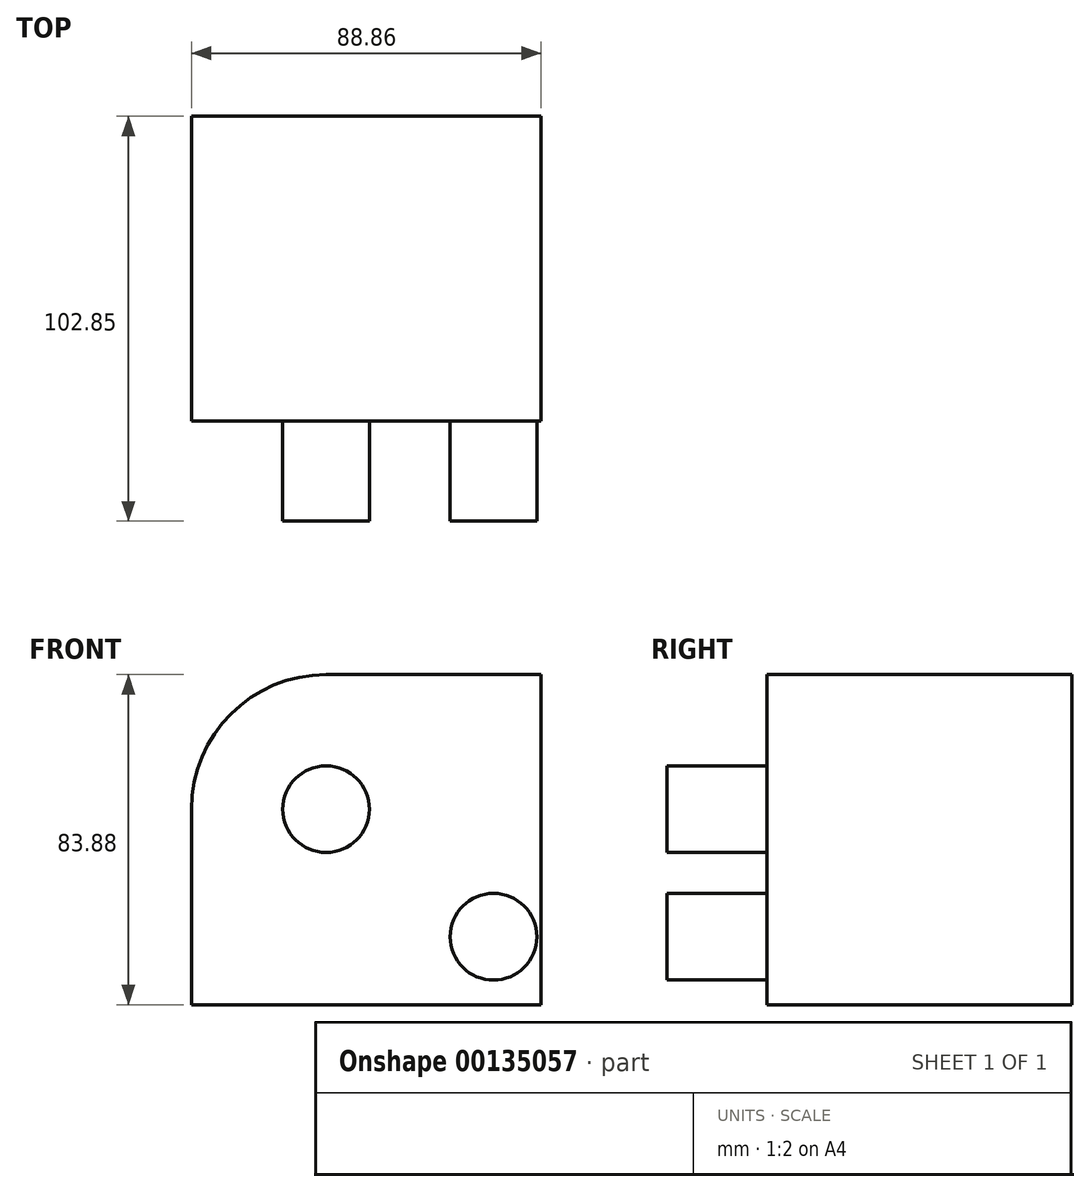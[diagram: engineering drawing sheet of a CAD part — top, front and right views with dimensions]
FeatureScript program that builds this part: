
annotation { "Feature Type Name" : "Feature", "Feature Type Description" : "" }
export const myFeature = defineFeature(function(context is Context, id is Id, definition is map)
    precondition{}
    {
        {
            var Q0;
            Q0=qCreatedBy(makeId("Front.planeOp"),FACE);
            var sketch = newSketch(context, id + "F0", { "sketchPlane" : qUnion([Q0])});
            skLineSegment(sketch, "E0.bottom", {"start": v(-44.43, 41.94) * mm, "end": v(44.43, 41.94) * mm});
            skLineSegment(sketch, "E0.top", {"start": v(-44.43, -41.94) * mm, "end": v(44.43, -41.94) * mm});
            skLineSegment(sketch, "E0.left", {"start": v(-44.43, 41.94) * mm, "end": v(-44.43, -41.94) * mm});
            skLineSegment(sketch, "E0.right", {"start": v(44.43, 41.94) * mm, "end": v(44.43, -41.94) * mm});
            skPoint(sketch, "E0.middle", {"position": v(0, 0) * mm});
            skSolve(sketch);
        }
        {
            var Q0;
            Q0=makeQuery(id+"F0.imprint","IMPRINT",FACE,{"disambiguationData":[TD([[makeQuery(id+"F0.imprint","IMPRINT",EDGE,{"derivedFrom":sQuery(id+"F0.wireOp",EDGE,"E0.bottom")}),-1.0]])]});
            extrude(context, id + "F1", {"entities" : qUnion([Q0]), "depth" : 77.45 * mm});
        }
        {
            var Q0;
            Q0=makeQuery(id+"F1.opExtrude","SWEPT_EDGE",EDGE,{"disambiguationData":[OSD([sQuery(id+"F0.wireOp",EDGE,"E0.bottom"),sQuery(id+"F0.wireOp",EDGE,"E0.left")])]});
            fillet(context, id + "F2", {"entities" : qUnion([Q0]), "radius" : 34.2 * mm, "tangentPropagation" : true, "allowEdgeOverflow" : false});
        }
        {
            var Q0;
            Q0=makeQuery(id+"F1.opExtrude","CAP_FACE",FACE,{"disambiguationData":[OSD([sQuery(id+"F0.wireOp",EDGE,"E0.bottom"),sQuery(id+"F0.wireOp",EDGE,"E0.top"),sQuery(id+"F0.wireOp",EDGE,"E0.left"),sQuery(id+"F0.wireOp",EDGE,"E0.right")])],"isStart":false});
            var sketch = newSketch(context, id + "F3", { "sketchPlane" : qUnion([Q0])});
            skArc(sketch, "E1.0", {"start": v(-44.43, 7.73) * mm, "mid": v(-34.41, 31.92) * mm, "end": v(-10.22, 41.94) * mm});
            skCircle(sketch, "E2", {"center": v(-10.22, 7.73) * mm, "radius": 11.02 * mm});
            skCircle(sketch, "E3", {"center": v(32.31, -24.68) * mm, "radius": 11.02 * mm});
            skSolve(sketch);
        }
        {
            var Q0;
            Q0=makeQuery(id+"F3.imprint","IMPRINT",FACE,{"disambiguationData":[TD([[makeQuery(id+"F3.imprint","IMPRINT",EDGE,{"derivedFrom":sQuery(id+"F3.wireOp",EDGE,"E2")}),1.0]])]});
            var Q1;
            Q1=makeQuery(id+"F3.imprint","IMPRINT",FACE,{"disambiguationData":[TD([[makeQuery(id+"F3.imprint","IMPRINT",EDGE,{"derivedFrom":sQuery(id+"F3.wireOp",EDGE,"E3")}),1.0]])]});
            extrude(context, id + "F4", {"entities" : qUnion([Q0, Q1]), "operationType" : NewBodyOperationType.ADD, "depth" : 25.4 * mm});
        }
    });
